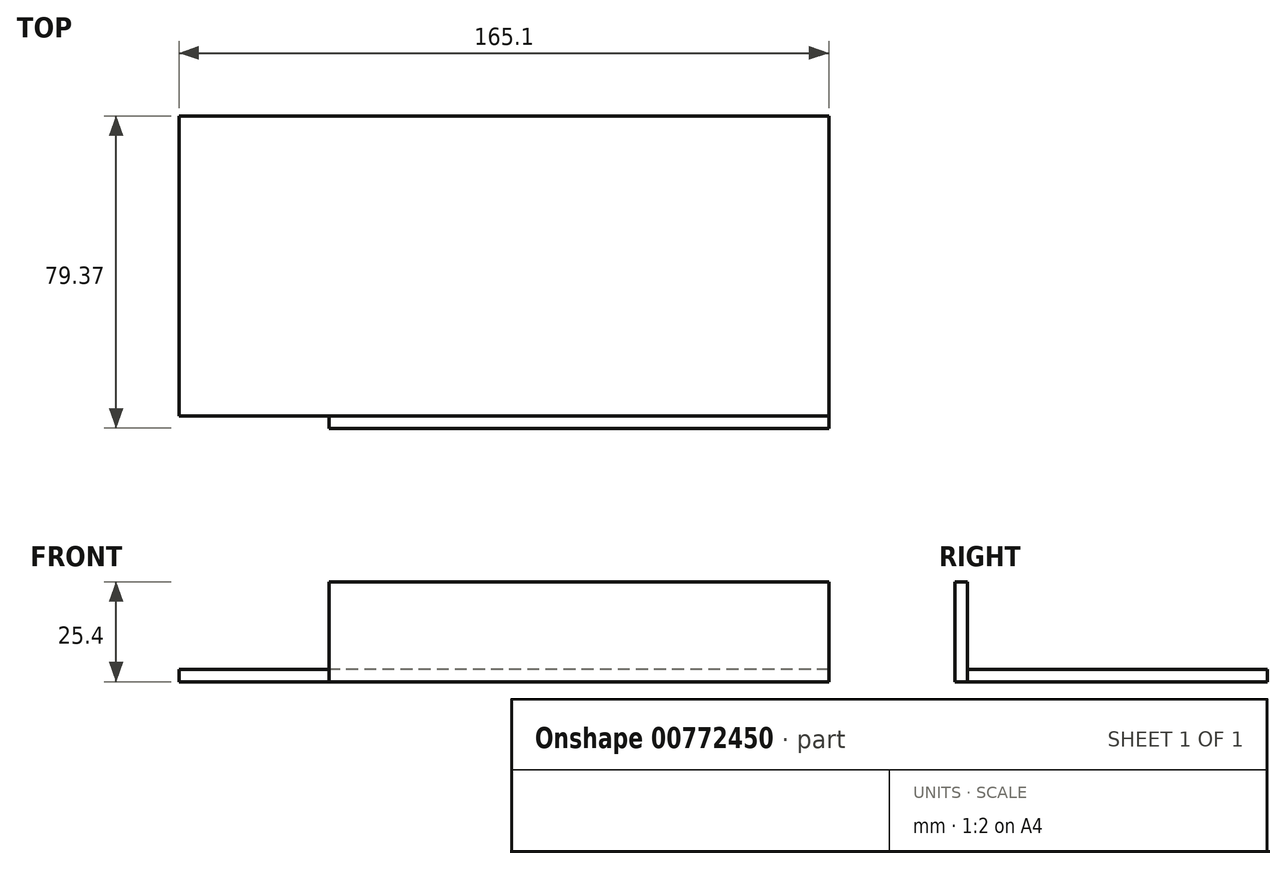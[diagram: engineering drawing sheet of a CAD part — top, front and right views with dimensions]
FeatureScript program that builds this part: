
annotation { "Feature Type Name" : "Feature", "Feature Type Description" : "" }
export const myFeature = defineFeature(function(context is Context, id is Id, definition is map)
    precondition{}
    {
        {
            var Q0;
            Q0=qCreatedBy(makeId("Top.planeOp"),FACE);
            var sketch = newSketch(context, id + "F0", { "sketchPlane" : qUnion([Q0])});
            skLineSegment(sketch, "E0.bottom", {"start": v(0, 0) * mm, "end": v(-165.1, 0) * mm});
            skLineSegment(sketch, "E0.top", {"start": v(0, 76.2) * mm, "end": v(-165.1, 76.2) * mm});
            skLineSegment(sketch, "E0.left", {"start": v(0, 0) * mm, "end": v(0, 76.2) * mm});
            skLineSegment(sketch, "E0.right", {"start": v(-165.1, 0) * mm, "end": v(-165.1, 76.2) * mm});
            skSolve(sketch);
        }
        {
            var Q0;
            Q0 = qSketchRegion(id + "F0", true);
            extrude(context, id + "F1", {"entities" : qUnion([Q0]), "depth" : 3.17 * mm, "offsetDistance" : 25.4 * mm});
        }
        {
            var Q0;
            Q0=makeQuery(id+"F1.opExtrude","SWEPT_FACE",FACE,{"disambiguationData":[OSD([sQuery(id+"F0.wireOp",EDGE,"E0.bottom")])]});
            var sketch = newSketch(context, id + "F2", { "sketchPlane" : qUnion([Q0])});
            skLineSegment(sketch, "E1.bottom", {"start": v(0, 0) * mm, "end": v(-127, 0) * mm});
            skLineSegment(sketch, "E1.top", {"start": v(0, 25.4) * mm, "end": v(-127, 25.4) * mm});
            skLineSegment(sketch, "E1.left", {"start": v(0, 0) * mm, "end": v(0, 25.4) * mm});
            skLineSegment(sketch, "E1.right", {"start": v(-127, 0) * mm, "end": v(-127, 25.4) * mm});
            skSolve(sketch);
        }
        {
            var Q0;
            Q0 = qSketchRegion(id + "F2", true);
            extrude(context, id + "F3", {"entities" : qUnion([Q0]), "depth" : 3.17 * mm, "offsetDistance" : 25.4 * mm});
        }
    });
